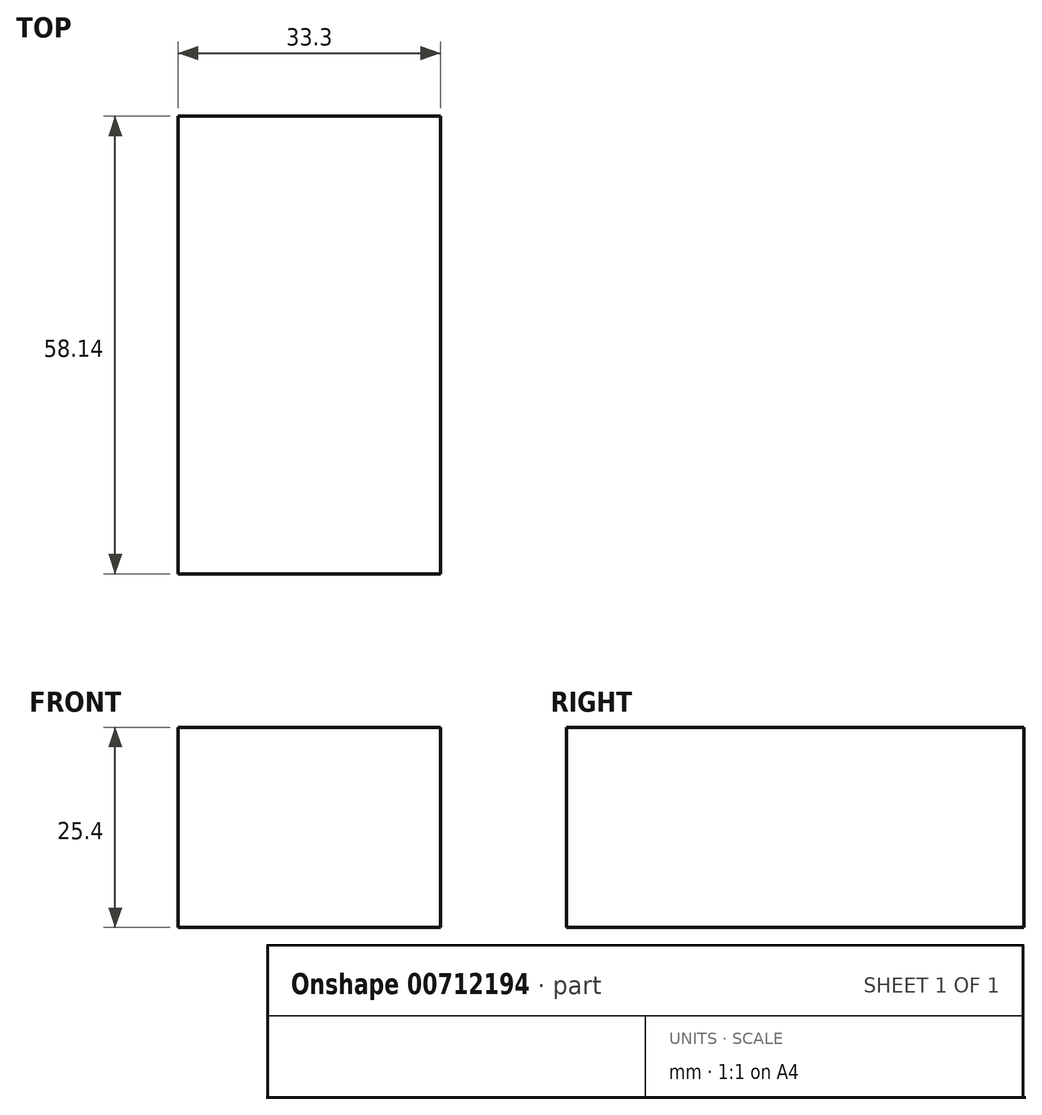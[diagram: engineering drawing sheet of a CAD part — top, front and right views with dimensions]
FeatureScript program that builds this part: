
annotation { "Feature Type Name" : "Feature", "Feature Type Description" : "" }
export const myFeature = defineFeature(function(context is Context, id is Id, definition is map)
    precondition{}
    {
        {
            var Q0;
            Q0=qCreatedBy(makeId("Top.planeOp"),FACE);
            var sketch = newSketch(context, id + "F0", { "sketchPlane" : qUnion([Q0])});
            skLineSegment(sketch, "E0.bottom", {"start": v(-16.65, 29.07) * mm, "end": v(16.65, 29.07) * mm});
            skLineSegment(sketch, "E0.top", {"start": v(-16.65, -29.07) * mm, "end": v(16.65, -29.07) * mm});
            skLineSegment(sketch, "E0.left", {"start": v(-16.65, 29.07) * mm, "end": v(-16.65, -29.07) * mm});
            skLineSegment(sketch, "E0.right", {"start": v(16.65, 29.07) * mm, "end": v(16.65, -29.07) * mm});
            skPoint(sketch, "E0.middle", {"position": v(0, 0) * mm});
            skSolve(sketch);
        }
        {
            var Q0;
            Q0 = qSketchRegion(id + "F0", true);
            extrude(context, id + "F1", {"entities" : qUnion([Q0]), "depth" : 25.4 * mm, "offsetDistance" : 25.4 * mm});
        }
    });
